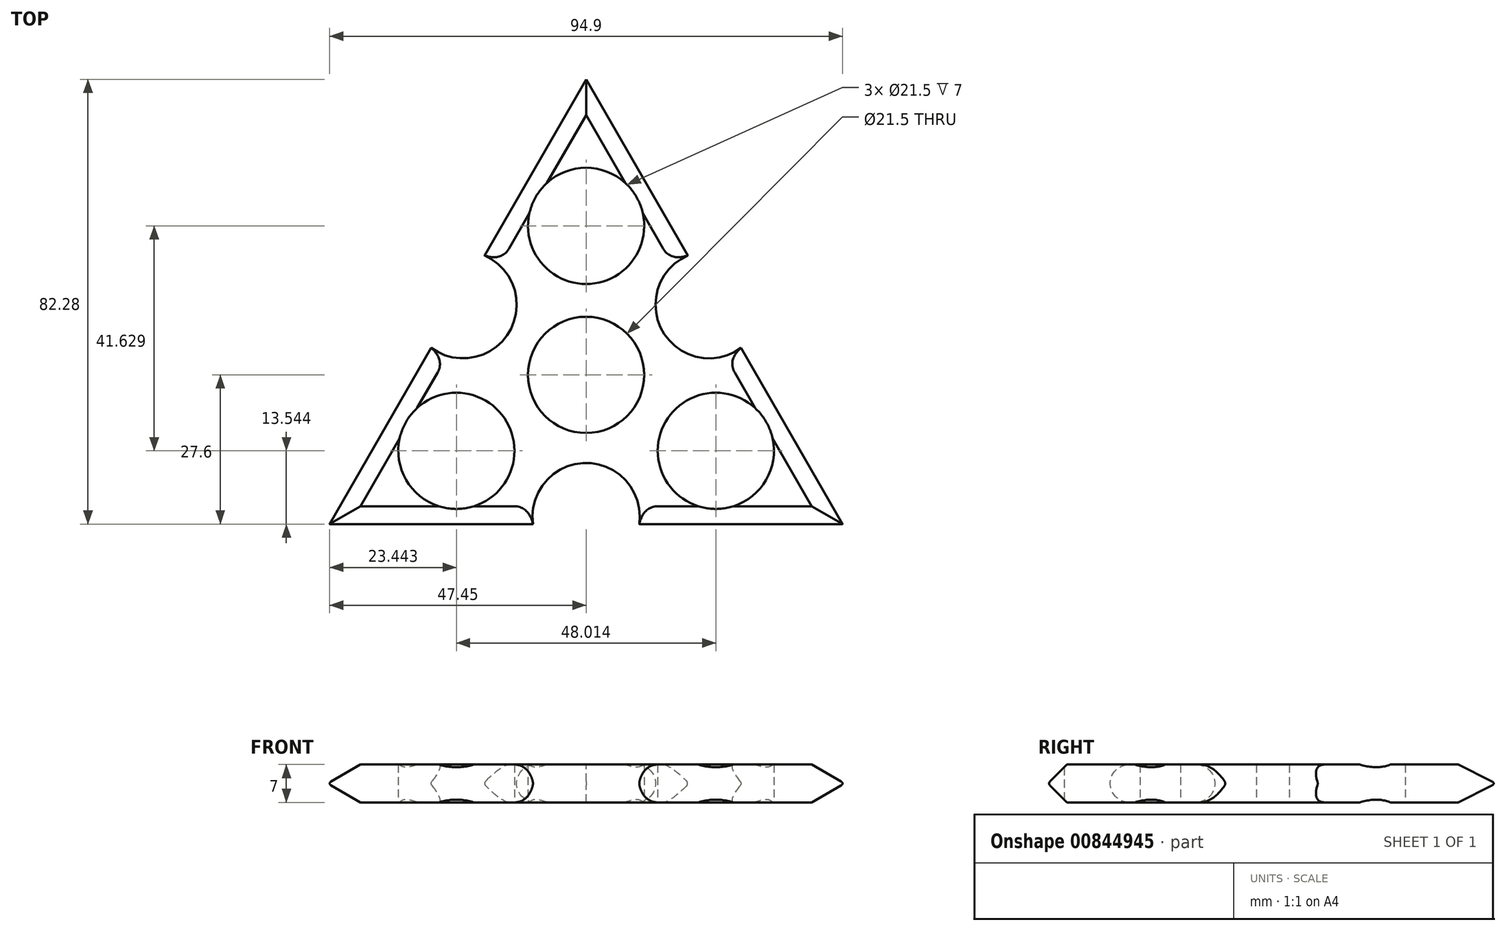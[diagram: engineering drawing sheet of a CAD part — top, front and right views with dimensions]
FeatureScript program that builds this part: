
annotation { "Feature Type Name" : "Feature", "Feature Type Description" : "" }
export const myFeature = defineFeature(function(context is Context, id is Id, definition is map)
    precondition{}
    {
        {
            var Q0;
            Q0=qCreatedBy(makeId("Top.planeOp"),FACE);
            var sketch = newSketch(context, id + "F0", { "sketchPlane" : qUnion([Q0])});
            skCircle(sketch, "E0", {"center": v(0, 0) * mm, "radius": 10.75 * mm});
            skCircle(sketch, "E1", {"center": v(0, 27.57) * mm, "radius": 10.75 * mm});
            skCircle(sketch, "E2.1.0", {"center": v(-24, -14.06) * mm, "radius": 10.75 * mm});
            skCircle(sketch, "E2.2.0", {"center": v(24, -14.06) * mm, "radius": 10.75 * mm});
            skPoint(sketch, "E3.center.orphan", {"position": v(-22.78, 13) * mm});
            skLineSegment(sketch, "E4", {"start": v(0, 55.1) * mm, "end": v(-18.99, 22.17) * mm});
            skLineSegment(sketch, "E5", {"start": v(-47.8, -27.8) * mm, "end": v(-9.8, -27.8) * mm});
            skLineSegment(sketch, "E6", {"start": v(47.8, -27.8) * mm, "end": v(28.82, 5.12) * mm});
            skArc(sketch, "E7", {"start": v(-28.82, 5.12) * mm, "mid": v(-14.17, 8.03) * mm, "end": v(-18.99, 22.17) * mm});
            skArc(sketch, "E8.1.0", {"start": v(9.8, -27.8) * mm, "mid": v(0, -16.3) * mm, "end": v(-9.8, -27.8) * mm});
            skArc(sketch, "E8.2.0", {"start": v(18.99, 22.17) * mm, "mid": v(14.17, 8.03) * mm, "end": v(28.82, 5.12) * mm});
            skPoint(sketch, "E8.center", {"position": v(0, -0.17) * mm});
            skLineSegment(sketch, "E9.trimOffspring", {"start": v(-28.82, 5.12) * mm, "end": v(-47.8, -27.8) * mm});
            skLineSegment(sketch, "E10.trimOffspring", {"start": v(18.99, 22.17) * mm, "end": v(0, 55.1) * mm});
            skLineSegment(sketch, "E11.trimOffspring", {"start": v(9.8, -27.8) * mm, "end": v(47.8, -27.8) * mm});
            skSolve(sketch);
        }
        {
            var Q0;
            Q0=makeQuery(id+"F0.imprint","IMPRINT",FACE,{"disambiguationData":[TD([[makeQuery(id+"F0.imprint","IMPRINT",EDGE,{"derivedFrom":sQuery(id+"F0.wireOp",EDGE,"E0")}),-1.0]])]});
            extrude(context, id + "F1", {"entities" : qUnion([Q0]), "depth" : 7 * mm, "offsetDistance" : 25 * mm});
        }
        {
            var Q0;
            Q0=makeQuery(id+"F1.opExtrude","CAP_EDGE",EDGE,{"disambiguationData":[OSD([sQuery(id+"F0.wireOp",EDGE,"E9.trimOffspring")])],"isStart":true});
            var Q1;
            Q1=makeQuery(id+"F1.opExtrude","CAP_EDGE",EDGE,{"disambiguationData":[OSD([sQuery(id+"F0.wireOp",EDGE,"E5")])],"isStart":true});
            var Q2;
            Q2=makeQuery(id+"F1.opExtrude","CAP_EDGE",EDGE,{"disambiguationData":[OSD([sQuery(id+"F0.wireOp",EDGE,"E11.trimOffspring")])],"isStart":true});
            var Q3;
            Q3=makeQuery(id+"F1.opExtrude","CAP_EDGE",EDGE,{"disambiguationData":[OSD([sQuery(id+"F0.wireOp",EDGE,"E6")])],"isStart":true});
            var Q4;
            Q4=makeQuery(id+"F1.opExtrude","CAP_EDGE",EDGE,{"disambiguationData":[OSD([sQuery(id+"F0.wireOp",EDGE,"E10.trimOffspring")])],"isStart":true});
            var Q5;
            Q5=makeQuery(id+"F1.opExtrude","CAP_EDGE",EDGE,{"disambiguationData":[OSD([sQuery(id+"F0.wireOp",EDGE,"E4")])],"isStart":true});
            var Q6;
            Q6=makeQuery(id+"F1.opExtrude","CAP_EDGE",EDGE,{"disambiguationData":[OSD([sQuery(id+"F0.wireOp",EDGE,"E10.trimOffspring")])],"isStart":false});
            var Q7;
            Q7=makeQuery(id+"F1.opExtrude","CAP_EDGE",EDGE,{"disambiguationData":[OSD([sQuery(id+"F0.wireOp",EDGE,"E4")])],"isStart":false});
            var Q8;
            Q8=makeQuery(id+"F1.opExtrude","CAP_EDGE",EDGE,{"disambiguationData":[OSD([sQuery(id+"F0.wireOp",EDGE,"E9.trimOffspring")])],"isStart":false});
            var Q9;
            Q9=makeQuery(id+"F1.opExtrude","CAP_EDGE",EDGE,{"disambiguationData":[OSD([sQuery(id+"F0.wireOp",EDGE,"E5")])],"isStart":false});
            var Q10;
            Q10=makeQuery(id+"F1.opExtrude","CAP_EDGE",EDGE,{"disambiguationData":[OSD([sQuery(id+"F0.wireOp",EDGE,"E11.trimOffspring")])],"isStart":false});
            var Q11;
            Q11=makeQuery(id+"F1.opExtrude","CAP_EDGE",EDGE,{"disambiguationData":[OSD([sQuery(id+"F0.wireOp",EDGE,"E6")])],"isStart":false});
            chamfer(context, id + "F2", {"entities" : qUnion([Q0, Q1, Q2, Q3, Q4, Q5, Q6, Q7, Q8, Q9, Q10, Q11]), "width" : 3.5 * mm, "tangentPropagation" : true});
        }
        {
            var Q0;
            Q0=makeQuery(id+"F1.opExtrude","CAP_EDGE",EDGE,{"disambiguationData":[OSD([sQuery(id+"F0.wireOp",EDGE,"E7")])],"isStart":true});
            var Q1;
            Q1=makeQuery(id+"F1.opExtrude","CAP_EDGE",EDGE,{"disambiguationData":[OSD([sQuery(id+"F0.wireOp",EDGE,"E8.1.0")])],"isStart":true});
            var Q2;
            Q2=makeQuery(id+"F1.opExtrude","CAP_EDGE",EDGE,{"disambiguationData":[OSD([sQuery(id+"F0.wireOp",EDGE,"E8.2.0")])],"isStart":true});
            var Q3;
            Q3=makeQuery(id+"F1.opExtrude","CAP_EDGE",EDGE,{"disambiguationData":[OSD([sQuery(id+"F0.wireOp",EDGE,"E8.2.0")])],"isStart":false});
            var Q4;
            Q4=makeQuery(id+"F1.opExtrude","CAP_EDGE",EDGE,{"disambiguationData":[OSD([sQuery(id+"F0.wireOp",EDGE,"E7")])],"isStart":false});
            var Q5;
            Q5=makeQuery(id+"F1.opExtrude","CAP_EDGE",EDGE,{"disambiguationData":[OSD([sQuery(id+"F0.wireOp",EDGE,"E8.1.0")])],"isStart":false});
            fillet(context, id + "F3", {"entities" : qUnion([Q0, Q1, Q2, Q3, Q4, Q5]), "radius" : 3.5 * mm, "tangentPropagation" : true, "allowEdgeOverflow" : false});
        }
        {
            var Q0;
            {var subQ0=sQuery(id+"F0.wireOp",EDGE,"E5");Q0=makeQuery(id+"F2.opChamfer","BLEND_EDGE",EDGE,{"blendedFrom":[makeQuery(id+"F1.opExtrude","CAP_EDGE",EDGE,{"disambiguationData":[OSD([subQ0])],"isStart":true}),makeQuery(id+"F1.opExtrude","CAP_EDGE",EDGE,{"disambiguationData":[OSD([subQ0])],"isStart":false})],"blendedInto":[]});}
            var Q1;
            {var subQ0=sQuery(id+"F0.wireOp",EDGE,"E11.trimOffspring");Q1=makeQuery(id+"F2.opChamfer","BLEND_EDGE",EDGE,{"blendedFrom":[makeQuery(id+"F1.opExtrude","CAP_EDGE",EDGE,{"disambiguationData":[OSD([subQ0])],"isStart":true}),makeQuery(id+"F1.opExtrude","CAP_EDGE",EDGE,{"disambiguationData":[OSD([subQ0])],"isStart":false})],"blendedInto":[]});}
            var Q2;
            {var subQ0=sQuery(id+"F0.wireOp",EDGE,"E6");Q2=makeQuery(id+"F2.opChamfer","BLEND_EDGE",EDGE,{"blendedFrom":[makeQuery(id+"F1.opExtrude","CAP_EDGE",EDGE,{"disambiguationData":[OSD([subQ0])],"isStart":true}),makeQuery(id+"F1.opExtrude","CAP_EDGE",EDGE,{"disambiguationData":[OSD([subQ0])],"isStart":false})],"blendedInto":[]});}
            var Q3;
            {var subQ0=sQuery(id+"F0.wireOp",EDGE,"E10.trimOffspring");Q3=makeQuery(id+"F2.opChamfer","BLEND_EDGE",EDGE,{"blendedFrom":[makeQuery(id+"F1.opExtrude","CAP_EDGE",EDGE,{"disambiguationData":[OSD([subQ0])],"isStart":true}),makeQuery(id+"F1.opExtrude","CAP_EDGE",EDGE,{"disambiguationData":[OSD([subQ0])],"isStart":false})],"blendedInto":[]});}
            var Q4;
            {var subQ0=sQuery(id+"F0.wireOp",EDGE,"E4");Q4=makeQuery(id+"F2.opChamfer","BLEND_EDGE",EDGE,{"blendedFrom":[makeQuery(id+"F1.opExtrude","CAP_EDGE",EDGE,{"disambiguationData":[OSD([subQ0])],"isStart":true}),makeQuery(id+"F1.opExtrude","CAP_EDGE",EDGE,{"disambiguationData":[OSD([subQ0])],"isStart":false})],"blendedInto":[]});}
            var Q5;
            {var subQ0=sQuery(id+"F0.wireOp",EDGE,"E9.trimOffspring");Q5=makeQuery(id+"F2.opChamfer","BLEND_EDGE",EDGE,{"blendedFrom":[makeQuery(id+"F1.opExtrude","CAP_EDGE",EDGE,{"disambiguationData":[OSD([subQ0])],"isStart":true}),makeQuery(id+"F1.opExtrude","CAP_EDGE",EDGE,{"disambiguationData":[OSD([subQ0])],"isStart":false})],"blendedInto":[]});}
            fillet(context, id + "F4", {"entities" : qUnion([Q0, Q1, Q2, Q3, Q4, Q5]), "radius" : .5 * mm, "tangentPropagation" : true, "allowEdgeOverflow" : false});
        }
    });
